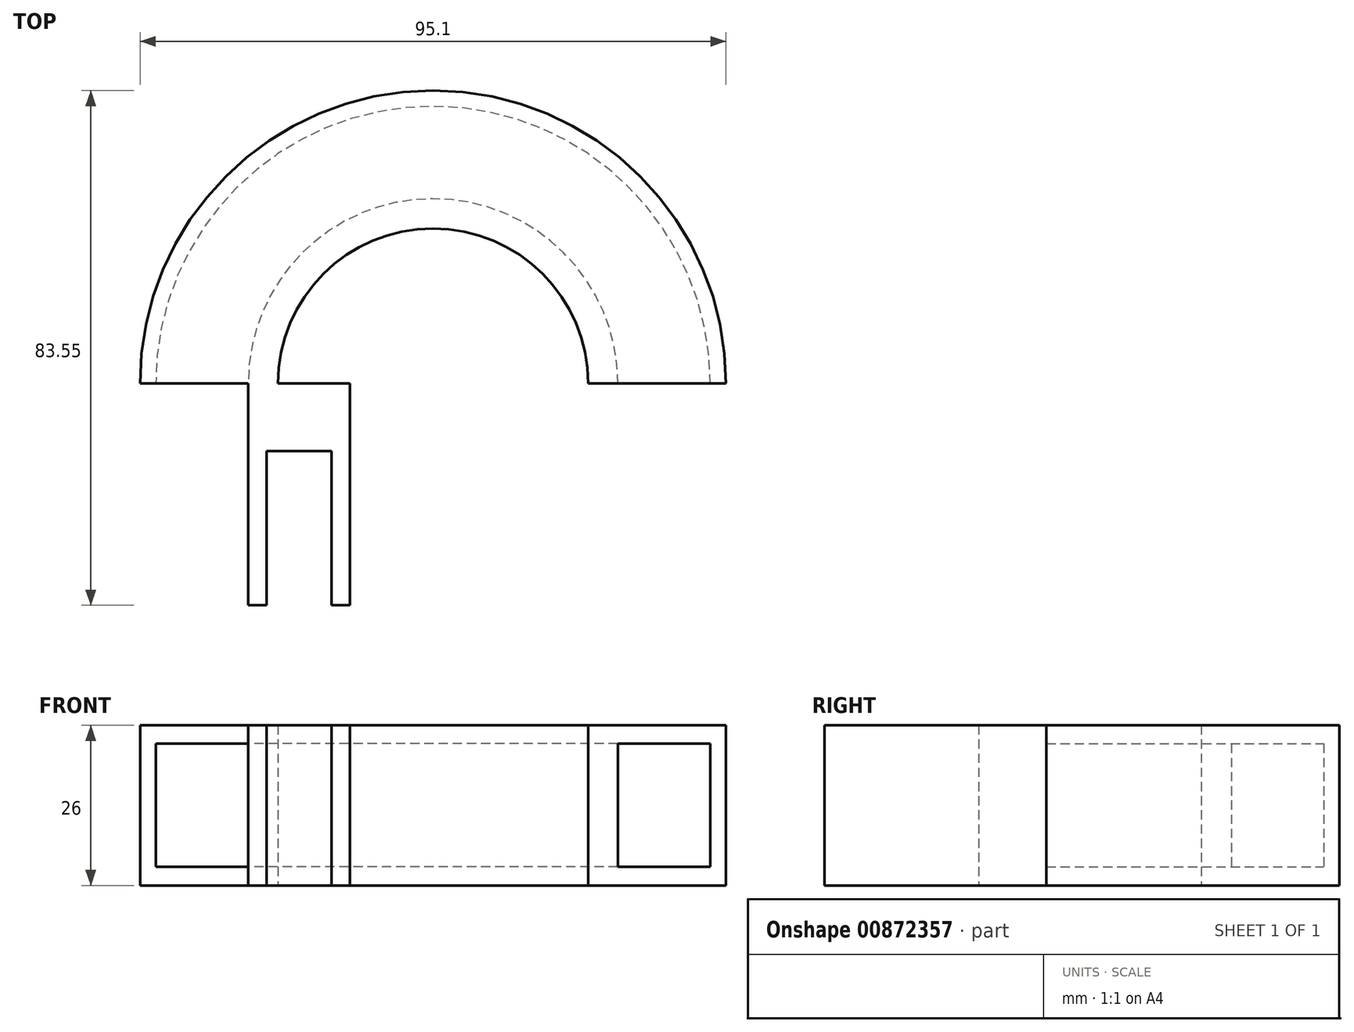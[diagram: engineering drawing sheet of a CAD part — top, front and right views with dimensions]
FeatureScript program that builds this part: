
annotation { "Feature Type Name" : "Feature", "Feature Type Description" : "" }
export const myFeature = defineFeature(function(context is Context, id is Id, definition is map)
    precondition{}
    {
        {
            var Q0;
            Q0=qCreatedBy(makeId("Top.planeOp"),FACE);
            var sketch = newSketch(context, id + "F0", { "sketchPlane" : qUnion([Q0])});
            skCircle(sketch, "E0", {"center": v(0, 0) * mm, "radius": 25.17 * mm});
            skCircle(sketch, "E1", {"center": v(0, 0) * mm, "radius": 30 * mm});
            skCircle(sketch, "E2", {"center": v(0, 0) * mm, "radius": 45 * mm});
            skSolve(sketch);
        }
        {
            var Q0;
            Q0=makeQuery(id+"F0.imprint","IMPRINT",FACE,{"disambiguationData":[TD([[makeQuery(id+"F0.imprint","IMPRINT",EDGE,{"derivedFrom":sQuery(id+"F0.wireOp",EDGE,"E0")}),-1.0]])]});
            extrude(context, id + "F1", {"entities" : qUnion([Q0]), "depth" : 26 * mm, "offsetDistance" : 25.4 * mm});
        }
        {
            var Q0;
            Q0 = qSketchRegion(id + "F0", true);
            extrude(context, id + "F2", {"entities" : qUnion([Q0]), "operationType" : NewBodyOperationType.ADD, "depth" : 3 * mm, "offsetDistance" : 25 * mm});
        }
        {
            var Q0;
            Q0=makeQuery(id+"F1.opExtrude","CAP_FACE",FACE,{"disambiguationData":[OSD([sQuery(id+"F0.wireOp",EDGE,"E0"),sQuery(id+"F0.wireOp",EDGE,"E1")])],"isStart":false});
            var sketch = newSketch(context, id + "F3", { "sketchPlane" : qUnion([Q0])});
            skCircle(sketch, "E3", {"center": v(0, 0) * mm, "radius": 45 * mm});
            skSolve(sketch);
        }
        {
            var Q0;
            Q0=makeQuery(id+"F3.imprint","IMPRINT",FACE,{"disambiguationData":[TD([[makeQuery(id+"F3.imprint","IMPRINT",EDGE,{"derivedFrom":sQuery(id+"F3.wireOp",EDGE,"E3")}),1.0]])]});
            extrude(context, id + "F4", {"entities" : qUnion([Q0]), "operationType" : NewBodyOperationType.ADD, "oppositeDirection" : true, "depth" : 3 * mm, "offsetDistance" : 25 * mm});
        }
        {
            var Q0;
            {var subQ0=sQuery(id+"F0.wireOp",EDGE,"E1");Q0=makeQuery(id+"F2.boolean.opBoolean","MERGE",FACE,{"derivedFrom":[makeQuery(id+"F1.opExtrude","CAP_FACE",FACE,{"disambiguationData":[OSD([sQuery(id+"F0.wireOp",EDGE,"E0"),subQ0])],"isStart":true}),makeQuery(id+"F2.opExtrude","CAP_FACE",FACE,{"disambiguationData":[OSD([subQ0,sQuery(id+"F0.wireOp",EDGE,"E2")])],"isStart":true})]});}
            var sketch = newSketch(context, id + "F5", { "sketchPlane" : qUnion([Q0])});
            skCircle(sketch, "E4", {"center": v(0, 0) * mm, "radius": 47.55 * mm});
            skSolve(sketch);
        }
        {
            var Q0;
            Q0=makeQuery(id+"F5.imprint","IMPRINT",FACE,{"disambiguationData":[TD([[makeQuery(id+"F5.imprint","IMPRINT",EDGE,{"derivedFrom":sQuery(id+"F5.wireOp",EDGE,"E4")}),1.0]])]});
            extrude(context, id + "F6", {"entities" : qUnion([Q0]), "operationType" : NewBodyOperationType.ADD, "oppositeDirection" : true, "depth" : 26 * mm, "offsetDistance" : 25 * mm});
        }
        {
            var Q0;
            {var subQ0=sQuery(id+"F0.wireOp",EDGE,"E2");var subQ1=sQuery(id+"F0.wireOp",EDGE,"E1");Q0=makeQuery(id+"F6.boolean.opBoolean","MERGE",FACE,{"derivedFrom":[makeQuery(id+"F2.boolean.opBoolean","MERGE",FACE,{"derivedFrom":[makeQuery(id+"F1.opExtrude","CAP_FACE",FACE,{"disambiguationData":[OSD([sQuery(id+"F0.wireOp",EDGE,"E0"),subQ1])],"isStart":true}),makeQuery(id+"F2.opExtrude","CAP_FACE",FACE,{"disambiguationData":[OSD([subQ1,subQ0])],"isStart":true})]}),makeQuery(id+"F6.opExtrude","CAP_FACE",FACE,{"disambiguationData":[OSD([subQ0,sQuery(id+"F5.wireOp",EDGE,"E4")])],"isStart":true})]});}
            var sketch = newSketch(context, id + "F7", { "sketchPlane" : qUnion([Q0])});
            skLineSegment(sketch, "E5", {"start": v(47.55, 0) * mm, "end": v(-47.55, 0) * mm});
            skSolve(sketch);
        }
        {
            var Q0;
            Q0 = qSketchRegion(id + "F7", true);
            var Q1;
            {var subQ0=sQuery(id+"F7.wireOp",EDGE,"E5");var subQ1=makeQuery(id+"F6.opExtrude","CAP_EDGE",EDGE,{"disambiguationData":[OSD([sQuery(id+"F5.wireOp",EDGE,"E4")])],"isStart":true});var subQ2=makeQuery(id+"F7.imprint","INTERSECT",VERTEX,{"disambiguationData":[OD(0.0)],"derivedFrom":[subQ1,subQ0]});Q1=makeQuery(id+"F7.imprint","IMPRINT",FACE,{"disambiguationData":[TD([[makeQuery(id+"F7.imprint","IMPRINT",EDGE,{"disambiguationData":[TD([[subQ2,-1.0]])],"derivedFrom":subQ0}),-1.0]])]});}
            extrude(context, id + "F8", {"entities" : qUnion([Q0, Q1]), "operationType" : NewBodyOperationType.REMOVE, "oppositeDirection" : true, "depth" : 26 * mm, "offsetDistance" : 25 * mm});
        }
        {
            var Q0;
            {var subQ0=sQuery(id+"F7.wireOp",EDGE,"E5");Q0=makeQuery(id+"F8.boolean.opBoolean","COPY",FACE,{"derivedFrom":makeQuery(id+"F8.opExtrude","SWEPT_FACE",FACE,{"disambiguationData":[OSD([subQ0]),TDD([makeQuery(id+"F7.imprint","IMPRINT",EDGE,{"disambiguationData":[TD([[makeQuery(id+"F7.imprint","INTERSECT",VERTEX,{"disambiguationData":[OD(1.0)],"derivedFrom":[makeQuery(id+"F6.opExtrude","CAP_EDGE",EDGE,{"disambiguationData":[OSD([sQuery(id+"F5.wireOp",EDGE,"E4")])],"isStart":true}),subQ0]}),1.0]])],"derivedFrom":subQ0})])]})});}
            var sketch = newSketch(context, id + "F9", { "sketchPlane" : qUnion([Q0])});
            skLineSegment(sketch, "E6.bottom", {"start": v(-30, 26) * mm, "end": v(-13.5, 26) * mm});
            skLineSegment(sketch, "E6.top", {"start": v(-30, 0) * mm, "end": v(-13.5, 0) * mm});
            skLineSegment(sketch, "E6.left", {"start": v(-30, 26) * mm, "end": v(-30, 0) * mm});
            skLineSegment(sketch, "E6.right", {"start": v(-13.5, 26) * mm, "end": v(-13.5, 0) * mm});
            skLineSegment(sketch, "E7.bottom", {"start": v(-27, 26) * mm, "end": v(-16.5, 26) * mm});
            skLineSegment(sketch, "E7.top", {"start": v(-27, 0) * mm, "end": v(-16.5, 0) * mm});
            skLineSegment(sketch, "E7.left", {"start": v(-27, 26) * mm, "end": v(-27, 0) * mm});
            skLineSegment(sketch, "E7.right", {"start": v(-16.5, 26) * mm, "end": v(-16.5, 0) * mm});
            skPoint(sketch, "E7.middle", {"position": v(-21.75, 13) * mm});
            skSolve(sketch);
        }
        {
            var Q0;
            {var subQ4=sQuery(id+"F9.wireOp",EDGE,"E7.right");Q0=makeQuery(id+"F9.imprint","IMPRINT",FACE,{"disambiguationData":[TD([[makeQuery(id+"F9.imprint","IMPRINT",EDGE,{"derivedFrom":subQ4}),-1.0]])]});}
            var Q1;
            {var subQ2=sQuery(id+"F9.wireOp",EDGE,"E6.right");Q1=makeQuery(id+"F9.imprint","IMPRINT",FACE,{"disambiguationData":[TD([[makeQuery(id+"F9.imprint","IMPRINT",EDGE,{"derivedFrom":subQ2}),-1.0]])]});}
            var Q2;
            {var subQ4=sQuery(id+"F9.wireOp",EDGE,"E7.left");Q2=makeQuery(id+"F9.imprint","IMPRINT",FACE,{"disambiguationData":[TD([[makeQuery(id+"F9.imprint","IMPRINT",EDGE,{"derivedFrom":subQ4}),1.0]])]});}
            var Q3;
            {var subQ11=sQuery(id+"F9.wireOp",EDGE,"E7.left");Q3=makeQuery(id+"F9.imprint","IMPRINT",FACE,{"disambiguationData":[TD([[makeQuery(id+"F9.imprint","IMPRINT",EDGE,{"derivedFrom":subQ11}),-1.0]])]});}
            extrude(context, id + "F10", {"entities" : qUnion([Q0, Q1, Q2, Q3]), "operationType" : NewBodyOperationType.ADD, "depth" : 36 * mm, "offsetDistance" : 25 * mm});
        }
        {
            var Q0;
            Q0=makeQuery(id+"F10.opExtrude","CAP_FACE",FACE,{"disambiguationData":[OSD([sQuery(id+"F9.wireOp",EDGE,"E6.bottom"),sQuery(id+"F9.wireOp",EDGE,"E6.top"),sQuery(id+"F9.wireOp",EDGE,"E6.left"),sQuery(id+"F9.wireOp",EDGE,"E6.right"),sQuery(id+"F9.wireOp",EDGE,"E7.bottom"),sQuery(id+"F9.wireOp",EDGE,"E7.top")])],"isStart":false});
            var sketch = newSketch(context, id + "F11", { "sketchPlane" : qUnion([Q0])});
            skLineSegment(sketch, "E8", {"start": v(-30, 0) * mm, "end": v(-13.5, 0) * mm});
            skLineSegment(sketch, "E9.bottom", {"start": v(-16.5, 26) * mm, "end": v(-27, 26) * mm});
            skLineSegment(sketch, "E9.top", {"start": v(-16.5, 0) * mm, "end": v(-27, 0) * mm});
            skLineSegment(sketch, "E9.left", {"start": v(-16.5, 26) * mm, "end": v(-16.5, 0) * mm});
            skLineSegment(sketch, "E9.right", {"start": v(-27, 26) * mm, "end": v(-27, 0) * mm});
            skPoint(sketch, "E9.middle", {"position": v(-21.75, 13) * mm});
            skSolve(sketch);
        }
        {
            var Q0;
            Q0 = qSketchRegion(id + "F11", true);
            extrude(context, id + "F12", {"entities" : qUnion([Q0]), "operationType" : NewBodyOperationType.REMOVE, "oppositeDirection" : true, "depth" : 25 * mm, "offsetDistance" : 25 * mm});
        }
    });
